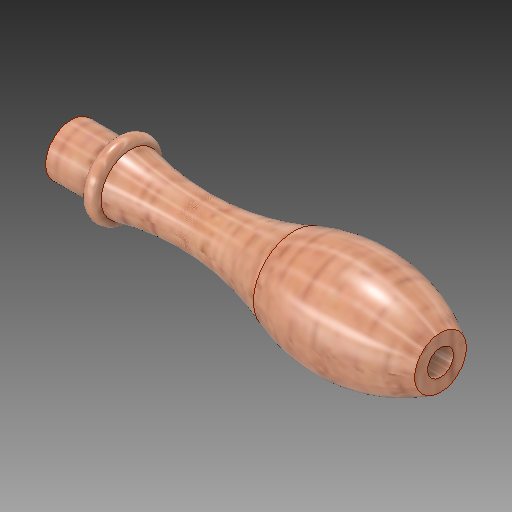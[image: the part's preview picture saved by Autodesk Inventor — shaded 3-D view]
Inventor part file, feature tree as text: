
AUTODESK INVENTOR PART (.ipt)
format: ipt  version: 2020 (Build 240168000, 168)  size: 262,144 bytes
history: native  units: in
note: dims shown in document units (in); Inventor stores cm internally (conversion verified against a paired STEP export)
features: revolve x1, sketch x1
ambient origin geometry x8: Origin, YZ Plane, XZ Plane, XY Plane, X Axis, Y Axis, Z Axis, Center Point
bodies: Solid1 (feature_tree)
feature tree (2):
  revolve  "Revolution1"  [1 undecoded]
  sketch  "Sketch1"  dims[d1=1.375in d3=0.4375in d5=0.0in d8=0.375in d10=1.0625in d13=2.375in d14=0.875in d16=0.375in d20=0.625in d21=2.3529in d22=1.375in d23=90.0deg d25=0.125in d27=3.125in d28=0.4375in d29=0.2188in]
note: 1 required parameter value undecoded (feature->parameter linkage not recoverable at this tier; creation-order binding heuristic only, values carry confidence <= 0.55)
